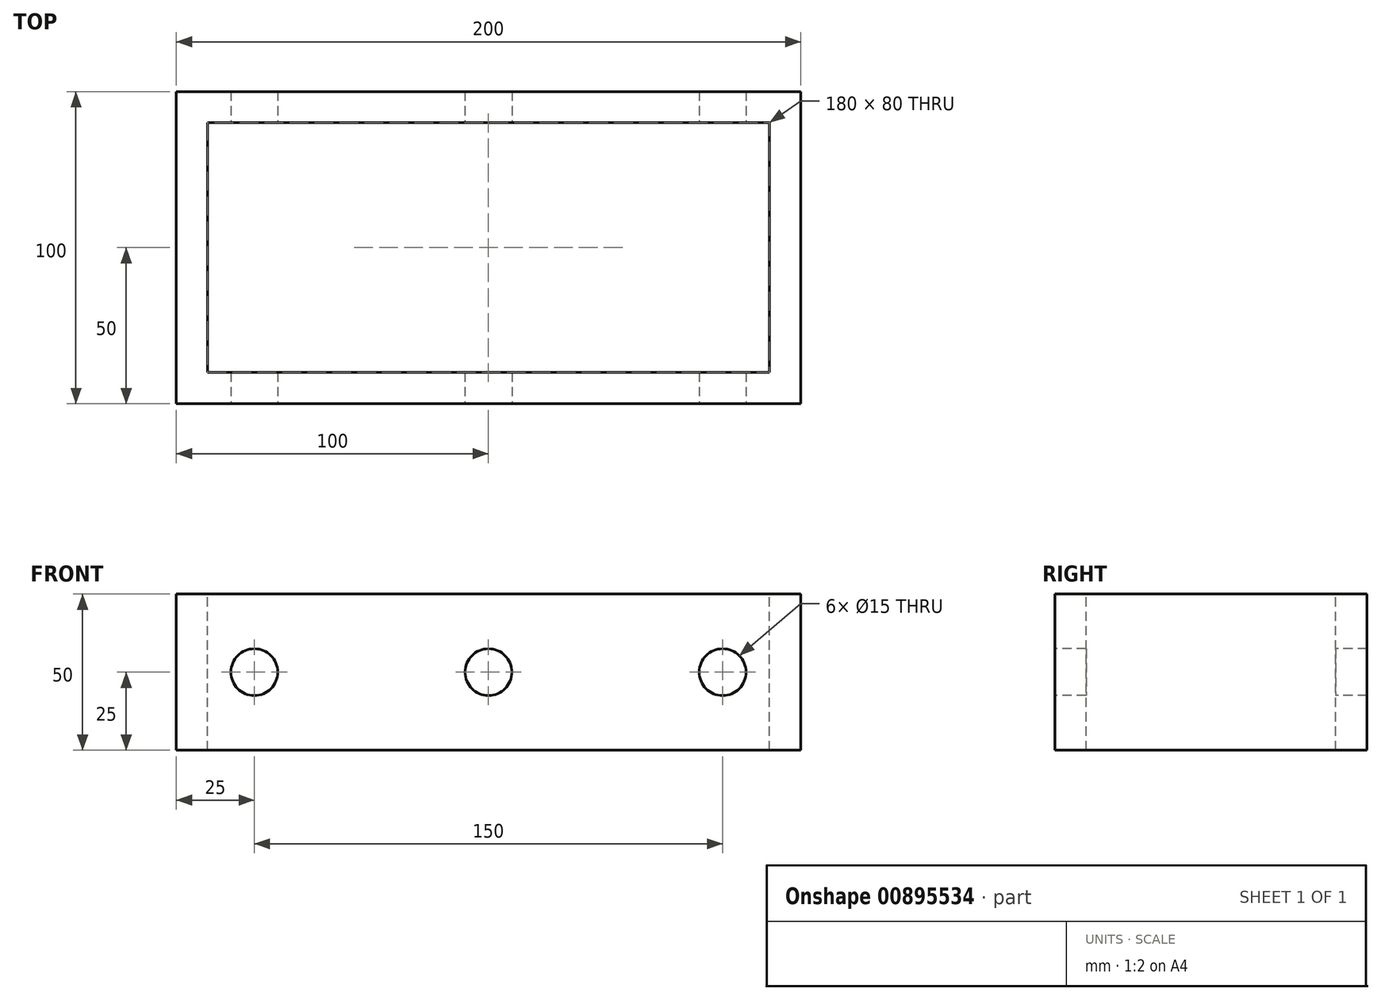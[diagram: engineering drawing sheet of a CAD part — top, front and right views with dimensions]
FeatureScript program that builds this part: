
annotation { "Feature Type Name" : "Feature", "Feature Type Description" : "" }
export const myFeature = defineFeature(function(context is Context, id is Id, definition is map)
    precondition{}
    {
        {
            var Q0;
            Q0=qCreatedBy(makeId("Top.planeOp"),FACE);
            var sketch = newSketch(context, id + "F0", { "sketchPlane" : qUnion([Q0])});
            skLineSegment(sketch, "E0.bottom", {"start": v(100, -50) * mm, "end": v(-100, -50) * mm});
            skLineSegment(sketch, "E0.top", {"start": v(100, 50) * mm, "end": v(-100, 50) * mm});
            skLineSegment(sketch, "E0.left", {"start": v(100, -50) * mm, "end": v(100, 50) * mm});
            skLineSegment(sketch, "E0.right", {"start": v(-100, -50) * mm, "end": v(-100, 50) * mm});
            skPoint(sketch, "E0.middle", {"position": v(0, 0) * mm});
            skLineSegment(sketch, "E1.bottom", {"start": v(90, -40) * mm, "end": v(-90, -40) * mm});
            skLineSegment(sketch, "E1.top", {"start": v(90, 40) * mm, "end": v(-90, 40) * mm});
            skLineSegment(sketch, "E1.left", {"start": v(90, -40) * mm, "end": v(90, 40) * mm});
            skLineSegment(sketch, "E1.right", {"start": v(-90, -40) * mm, "end": v(-90, 40) * mm});
            skSolve(sketch);
        }
        {
            var Q0;
            Q0=makeQuery(id+"F0.imprint","IMPRINT",FACE,{"disambiguationData":[TD([[makeQuery(id+"F0.imprint","IMPRINT",EDGE,{"derivedFrom":sQuery(id+"F0.wireOp",EDGE,"E0.bottom")}),-1.0]])]});
            extrude(context, id + "F1", {"entities" : qUnion([Q0]), "oppositeDirection" : true, "depth" : 50 * mm, "offsetDistance" : 25 * mm});
        }
        {
            var Q0;
            Q0=makeQuery(id+"F1.opExtrude","SWEPT_FACE",FACE,{"disambiguationData":[OSD([sQuery(id+"F0.wireOp",EDGE,"E0.bottom")])]});
            var sketch = newSketch(context, id + "F2", { "sketchPlane" : qUnion([Q0])});
            skCircle(sketch, "E2", {"center": v(-75, -25) * mm, "radius": 7.5 * mm});
            skCircle(sketch, "E3", {"center": v(0, -25) * mm, "radius": 7.5 * mm});
            skCircle(sketch, "E4", {"center": v(75, -25) * mm, "radius": 7.5 * mm});
            skSolve(sketch);
        }
        {
            var Q0;
            Q0=makeQuery(id+"F2.imprint","IMPRINT",FACE,{"disambiguationData":[TD([[makeQuery(id+"F2.imprint","IMPRINT",EDGE,{"derivedFrom":sQuery(id+"F2.wireOp",EDGE,"E3")}),1.0]])]});
            var Q1;
            Q1=makeQuery(id+"F2.imprint","IMPRINT",FACE,{"disambiguationData":[TD([[makeQuery(id+"F2.imprint","IMPRINT",EDGE,{"derivedFrom":sQuery(id+"F2.wireOp",EDGE,"E4")}),1.0]])]});
            var Q2;
            Q2=makeQuery(id+"F2.imprint","IMPRINT",FACE,{"disambiguationData":[TD([[makeQuery(id+"F2.imprint","IMPRINT",EDGE,{"derivedFrom":sQuery(id+"F2.wireOp",EDGE,"E2")}),1.0]])]});
            extrude(context, id + "F3", {"entities" : qUnion([Q0, Q1, Q2]), "operationType" : NewBodyOperationType.REMOVE, "oppositeDirection" : true, "depth" : 200 * mm, "offsetDistance" : 25 * mm});
        }
    });
